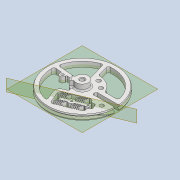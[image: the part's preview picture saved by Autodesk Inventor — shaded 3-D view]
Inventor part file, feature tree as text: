
AUTODESK INVENTOR PART (.ipt)
format: ipt  version: 2020 (Build 240168000, 168)  size: 1,970,176 bytes
history: native  units: mm
features: sketch x23, extrude x22, projected_geometry x20, fillet x16, thicken_offset x9, chamfer x6, other x4, pattern_linear x2, plane x2, reference x2, revolve x1, mirror x1
ambient origin geometry x8: Origin, YZ Plane, XZ Plane, XY Plane, X Axis, Y Axis, Z Axis, Center Point
bodies: Solid1 (feature_tree)
feature tree (108):
  extrude  "Extrusion1"  Depth=3.0mm TaperAngle=0.0deg
  revolve  "Revolution1"  [1 undecoded]
  extrude  "Extrusion2"  Depth=6.0mm
  extrude  "Extrusion3"  Depth=11.0mm
  extrude  "Extrusion4"  Depth=34.0mm
  extrude  "Extrusion5"  Depth=14.0mm
  chamfer  "Chamfer1"  Distance=5.0mm
  fillet  "Fillet1"  Radius=2.5mm
  fillet  "Fillet2"  Radius=15.0mm
  extrude  "Extrusion6"  Depth=0.5mm
  extrude  "Extrusion7"  TaperAngle=45.0deg  [1 undecoded]
  extrude  "Extrusion8"  Depth=12.0mm
  pattern_linear  "Rectangular Pattern1"  Count1=2  [1 undecoded]
  pattern_linear  "Rectangular Pattern2"  Spacing1=3.0mm  [1 undecoded]
  thicken_offset  "Thicken1"
  chamfer  "Chamfer2"  Distance=40.0mm
  plane  "Work Plane1"
  mirror  "Mirror1"
  extrude  "Extrusion9"  Depth=10.0mm
  fillet  "Fillet3"  Radius=1.0mm
  fillet  "Fillet4"  Radius=1.0mm
  fillet  "Fillet5"  Radius=1.0mm
  fillet  "Fillet6"  Radius=5.0mm
  extrude  "Extrusion10"  Depth=4.0mm
  fillet  "Fillet7"  Radius=3.0mm
  chamfer  "Chamfer3"  Distance=2.0mm
  extrude  "Extrusion11"  Depth=2.0mm
  fillet  "Fillet8"  Radius=1.0mm
  thicken_offset  "Thicken2"
  fillet  "Fillet9"  Radius=0.5mm
  extrude  "Extrusion12"  Depth=1.5mm
  thicken_offset  "Thicken3"
  thicken_offset  "Thicken4"
  chamfer  "Chamfer4"  Distance=3.0mm
  plane  "Work Plane2"
  extrude  "Extrusion13"  Depth=0.5mm
  chamfer  "Chamfer5"  Distance=3.0mm
  extrude  "Extrusion14"  Depth=0.5mm
  extrude  "Extrusion15"  Depth=0.5mm TaperAngle=45.0deg
  fillet  "Fillet10"  Radius=1.5mm
  fillet  "Fillet11"  Radius=1.4mm
  fillet  "Fillet12"  Radius=1.4mm
  thicken_offset  "Thicken5"
  thicken_offset  "Thicken6"
  thicken_offset  "Thicken7"
  extrude  "Extrusion16"  Depth=0.5mm TaperAngle=0.0deg
  extrude  "Extrusion17"  Depth=1.0mm
  extrude  "Extrusion18"  Depth=0.5mm
  extrude  "Extrusion19"  Depth=0.5mm
  thicken_offset  "Thicken8"
  thicken_offset  "Thicken9"
  extrude  "Extrusion20"  Depth=0.5mm
  fillet  "Fillet13"  Radius=7.3mm
  fillet  "Fillet14"  Radius=7.330383mm
  chamfer  "Chamfer6"  Distance=3.0mm
  fillet  "Fillet15"  Radius=3.0mm
  extrude  "Extrusion21"  Depth=0.5mm
  extrude  "Extrusion22"  Depth=0.5mm
  fillet  "Fillet16"  Radius=0.5mm
  sketch  "Sketch1"  dims[d0=50.0mm d1=3.0mm d2=0.0mm]
  sketch  "Sketch2"  dims[d3=1.5mm d4=1.5mm]
  projected_geometry  "Projected Loop1"
  sketch  "Sketch3"  dims[d5=90.0deg d6=6.0mm]
  sketch  "Sketch4"  dims[d7=3.0mm d8=0.0mm d9=11.0mm]
  projected_geometry  "Projected Loop2"
  sketch  "Sketch5"  dims[d10=5.0mm d11=0.0mm d12=34.0mm]
  projected_geometry  "Projected Loop3"
  sketch  "Sketch6"  dims[d13=3.0mm d14=14.0mm d15=5.0mm d16=0.0mm d17=2.5mm d18=15.0mm d19=0.0mm]
  projected_geometry  "Projected Loop4"
  sketch  "Sketch7"  dims[d20=0.5mm d21=2.0mm d22=45.0deg d23=0.5mm]
  projected_geometry  "Projected Loop5"
  sketch  "Sketch8"  dims[d24=1.0mm d25=45.0deg]
  projected_geometry  "Projected Loop6"
  sketch  "Sketch9"  dims[d26=3.0mm d27=12.0mm d28=20.0mm]
  projected_geometry  "Projected Loop7"
  projected_geometry  "Projected Loop8"
  sketch  "Sketch10"  dims[d29=15.0mm d30=0.0mm]
  projected_geometry  "Projected Loop9"
  sketch  "Sketch11"  dims[d31=4.0mm]
  projected_geometry  "Projected Loop10"
  sketch  "Sketch12"  dims[d32=4.0mm]
  projected_geometry  "Projected Loop11"
  sketch  "Sketch13"  dims[d33=2.0mm]
  projected_geometry  "Projected Loop12"
  sketch  "Sketch14"  dims[d34=14.0mm]
  reference  "Reference1"
  sketch  "Sketch15"  dims[d35=3.0mm d36=0.0mm]
  projected_geometry  "Projected Loop13"
  sketch  "Sketch16"  dims[d37=3.0mm]
  projected_geometry  "Projected Loop14"
  sketch  "Sketch17"  dims[d38=0.5mm]
  sketch  "Sketch18"  dims[d39=0.5mm]
  sketch  "Sketch19"  dims[d40=2.2mm]
  projected_geometry  "Projected Loop15"
  projected_geometry  "Projected Loop16"
  sketch  "Sketch20"  dims[d41=3.5mm]
  projected_geometry  "Projected Loop17"
  sketch  "Sketch21"  dims[d42=0.5mm]
  projected_geometry  "Projected Loop18"
  sketch  "Sketch22"  dims[d43=3.5mm]
  projected_geometry  "Projected Loop19"
  reference  "Reference2"
  sketch  "Sketch23"  dims[d44=0.5mm d45=3.0mm d46=0.0mm d47=40.0mm d49=1.3mm d50=20.0mm d52=10.0mm d53=1.0mm d54=1.0mm d55=1.0mm d56=2.0mm d57=45.0deg d58=5.0mm d59=4.0mm d60=3.0mm d61=0.0mm d62=2.0mm d63=2.0mm d64=1.0mm d65=0.5mm d66=1.5mm d67=3.0mm d68=3.0mm d69=3.0mm d70=0.0mm d71=0.2mm d72=0.5mm d73=2.0mm d74=45.0deg d75=1.5mm d76=1.4mm d77=1.4mm d78=3.0mm d79=0.0mm d80=1.0mm d81=5.0mm d82=5.0mm d83=0.5mm d84=7.3mm d85=7.330383mm d86=3.0mm d87=3.0mm d88=0.0mm d89=0.5mm d90=0.5mm d91=0.5mm d92=0.5mm d93=0.5mm d94=2.0mm d95=45.0deg d96=-2.0mm d97=1.0mm d98=4.5mm d99=0.0mm d100=1.0mm d101=2.0mm d102=45.0deg d103=6.108652mm d104=6.981317mm d105=10.0mm d106=3.1mm d107=10.0mm d108=3.1mm d109=4.5mm d110=0.0mm d111=18.0mm d112=46.0mm d113=2.5mm d114=2.5mm d115=2.5mm d116=2.5mm d117=26.0mm d118=3.0mm d119=4.712389mm d120=12.217305mm d121=4.5mm d122=0.0mm d123=4.0mm d124=1.0mm d125=1.5mm d126=2.0mm d127=2.0mm d128=2.0mm d129=2.0mm d130=1.0mm d131=1.0mm d132=4.5mm d133=0.0mm d134=3.0mm d135=4.5mm d136=0.0mm d137=12.0mm d138=25.481807mm d139=4.0mm d140=4.5mm d141=0.0mm d142=4.5mm d143=0.0mm d144=1.0mm d145=1.0mm d146=1.0mm d147=1.0mm d148=3.3mm d149=1.4mm d150=6.0mm d151=0.0mm d152=1.0mm d153=1.0mm d154=0.5mm d155=2.0mm d156=45.0deg d157=1.0mm d158=2.3mm d159=4.0mm d160=4.0mm d161=0.0mm d162=2.0mm d163=4.0mm d164=0.0mm d165=0.5mm]
  projected_geometry  "Projected Loop20"
  parser-record x1  (decoder bookkeeping rows leaked as tree rows — omitted from the tree; the rows remain in map.json)
  other  "driver_ass_1.iam"
  other  "bearing_3_6_2:1"
  other  "driver_wheel_1:1"
note: 4 required parameter values undecoded (feature->parameter linkage not recoverable at this tier; creation-order binding heuristic only, values carry confidence <= 0.55)
note: 1 file-system path scrubbed to <path> (originals preserved in map.json)